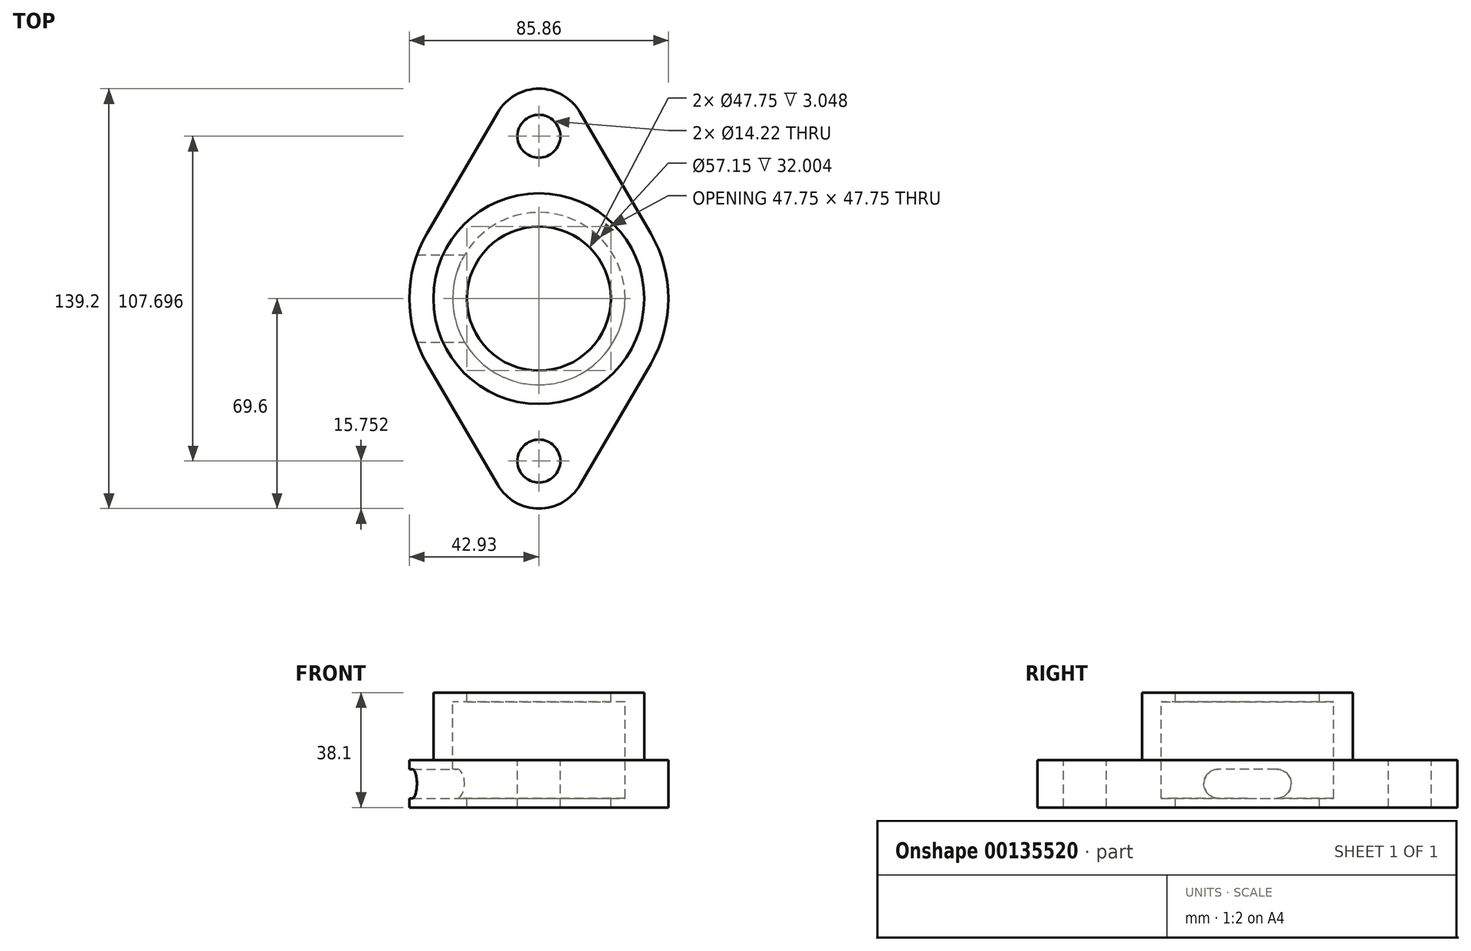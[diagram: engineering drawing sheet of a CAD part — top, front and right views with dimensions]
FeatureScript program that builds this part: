
annotation { "Feature Type Name" : "Feature", "Feature Type Description" : "" }
export const myFeature = defineFeature(function(context is Context, id is Id, definition is map)
    precondition{}
    {
        {
            var Q0;
            Q0=qCreatedBy(makeId("Top.planeOp"),FACE);
            var sketch = newSketch(context, id + "F0", { "sketchPlane" : qUnion([Q0])});
            skCircle(sketch, "E0", {"center": v(0, 0) * mm, "radius": 23.88 * mm});
            skArc(sketch, "E1", {"start": v(-37.06, 21.67) * mm, "mid": v(-42.93, 0) * mm, "end": v(-37.06, -21.67) * mm});
            skLineSegment(sketch, "E2", {"start": v(0, 0) * mm, "end": v(0, 53.85) * mm, "construction": true});
            skLineSegment(sketch, "E3", {"start": v(0, 0) * mm, "end": v(0, -53.85) * mm, "construction": true});
            skCircle(sketch, "E4", {"center": v(0, 53.85) * mm, "radius": 7.11 * mm});
            skArc(sketch, "E5", {"start": v(13.6, 61.8) * mm, "mid": v(0, 69.6) * mm, "end": v(-13.6, 61.8) * mm});
            skCircle(sketch, "E6", {"center": v(0, -53.85) * mm, "radius": 7.11 * mm});
            skArc(sketch, "E7", {"start": v(-13.6, -61.8) * mm, "mid": v(0, -69.6) * mm, "end": v(13.6, -61.8) * mm});
            skLineSegment(sketch, "E8", {"start": v(-13.6, 61.8) * mm, "end": v(-37.06, 21.67) * mm});
            skLineSegment(sketch, "E9", {"start": v(13.6, 61.8) * mm, "end": v(37.06, 21.67) * mm});
            skLineSegment(sketch, "E10", {"start": v(37.06, -21.67) * mm, "end": v(13.6, -61.8) * mm});
            skLineSegment(sketch, "E11", {"start": v(-13.6, -61.8) * mm, "end": v(-37.06, -21.67) * mm});
            skArc(sketch, "E12.trimOffspring", {"start": v(37.06, -21.67) * mm, "mid": v(42.93, 0) * mm, "end": v(37.06, 21.67) * mm});
            skSolve(sketch);
        }
        {
            var Q0;
            Q0 = qSketchRegion(id + "F0", true);
            extrude(context, id + "F1", {"entities" : qUnion([Q0]), "oppositeDirection" : true, "depth" : 15.75 * mm});
        }
        {
            var Q0;
            Q0=qCreatedBy(makeId("Top.planeOp"),FACE);
            var sketch = newSketch(context, id + "F2", { "sketchPlane" : qUnion([Q0])});
            skCircle(sketch, "E13", {"center": v(0, 0) * mm, "radius": 23.88 * mm});
            skCircle(sketch, "E14", {"center": v(0, 0) * mm, "radius": 34.93 * mm});
            skSolve(sketch);
        }
        {
            var Q0;
            Q0 = qSketchRegion(id + "F2", true);
            extrude(context, id + "F3", {"entities" : qUnion([Q0]), "operationType" : NewBodyOperationType.ADD, "depth" : 22.35 * mm});
        }
        {
            var Q0;
            Q0=qCreatedBy(makeId("Front.planeOp"),FACE);
            var sketch = newSketch(context, id + "F4", { "sketchPlane" : qUnion([Q0])});
            skLineSegment(sketch, "E15", {"start": v(0, 0) * mm, "end": v(0, -12.7) * mm, "construction": true});
            skLineSegment(sketch, "E16", {"start": v(0, 0) * mm, "end": v(0, 19.3) * mm, "construction": true});
            skLineSegment(sketch, "E17", {"start": v(28.58, 19.3) * mm, "end": v(28.58, -12.7) * mm});
            skLineSegment(sketch, "E18", {"start": v(28.58, -12.7) * mm, "end": v(0, -12.7) * mm});
            skLineSegment(sketch, "E19", {"start": v(0, -12.7) * mm, "end": v(0, 19.3) * mm});
            skLineSegment(sketch, "E20", {"start": v(28.58, 19.3) * mm, "end": v(0, 19.3) * mm});
            skSolve(sketch);
        }
        {
            var Q0;
            Q0 = qSketchRegion(id + "F4", true);
            var Q1;
            Q1=sQuery(id+"F4.wireOp",EDGE,"E19");
            revolve(context, id + "F5", {"operationType" : NewBodyOperationType.REMOVE, "entities" : qUnion([Q0]), "axis" : qUnion([Q1]), "revolveType" : RevolveType.FULL, "oppositeDirection" : true});
        }
        {
            var Q0;
            Q0=qCreatedBy(makeId("Right.planeOp"),FACE);
            var sketch = newSketch(context, id + "F6", { "sketchPlane" : qUnion([Q0])});
            skLineSegment(sketch, "E21", {"start": v(0, 0) * mm, "end": v(0, -7.87) * mm, "construction": true});
            skLineSegment(sketch, "E22", {"start": v(0, -7.87) * mm, "end": v(9.65, -7.87) * mm, "construction": true});
            skLineSegment(sketch, "E23", {"start": v(0, -7.87) * mm, "end": v(-9.65, -7.87) * mm, "construction": true});
            skArc(sketch, "E24", {"start": v(-9.65, -3.05) * mm, "mid": v(-14.48, -7.87) * mm, "end": v(-9.65, -12.7) * mm});
            skArc(sketch, "E25", {"start": v(9.65, -12.7) * mm, "mid": v(14.48, -7.87) * mm, "end": v(9.65, -3.05) * mm});
            skLineSegment(sketch, "E26", {"start": v(9.65, -3.05) * mm, "end": v(-9.65, -3.05) * mm});
            skLineSegment(sketch, "E27", {"start": v(-9.65, -12.7) * mm, "end": v(9.65, -12.7) * mm});
            skSolve(sketch);
        }
        {
            var Q0;
            Q0 = qSketchRegion(id + "F6", true);
            var Q1;
            Q1=makeQuery(id+"F1.opExtrude","SWEPT_FACE",FACE,{"disambiguationData":[OSD([sQuery(id+"F0.wireOp",EDGE,"E1")])]});
            extrude(context, id + "F7", {"entities" : qUnion([Q0]), "operationType" : NewBodyOperationType.REMOVE, "endBound" : BoundingType.UP_TO_SURFACE, "oppositeDirection" : true, "endBoundEntityFace" : qUnion([Q1]), "depth" : 25.4 * mm});
        }
    });
